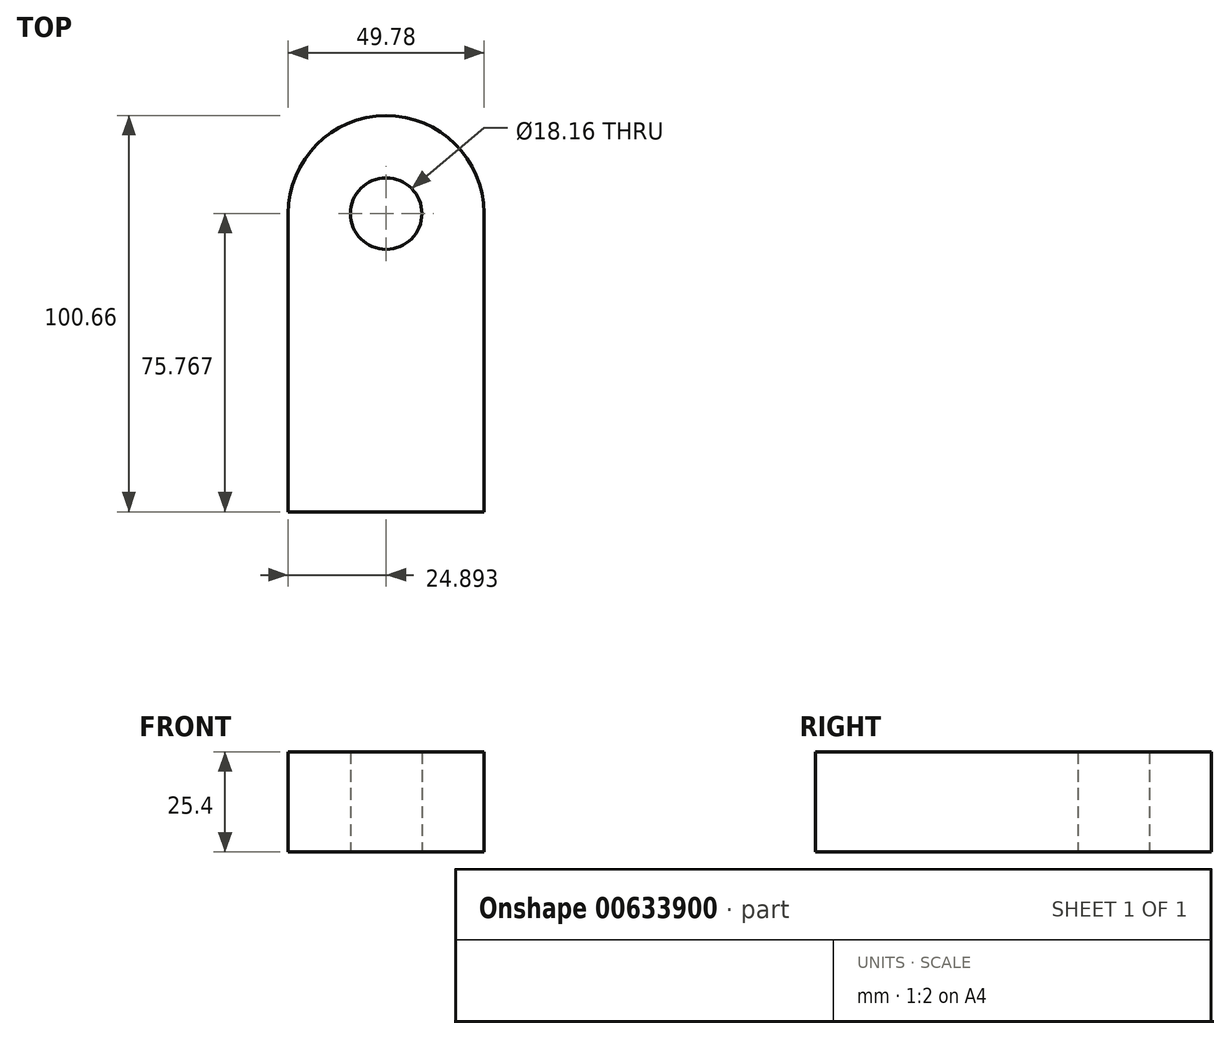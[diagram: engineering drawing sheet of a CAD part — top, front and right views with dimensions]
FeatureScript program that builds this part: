
annotation { "Feature Type Name" : "Feature", "Feature Type Description" : "" }
export const myFeature = defineFeature(function(context is Context, id is Id, definition is map)
    precondition{}
    {
        {
            var Q0;
            Q0=qCreatedBy(makeId("Top.planeOp"),FACE);
            var sketch = newSketch(context, id + "F0", { "sketchPlane" : qUnion([Q0])});
            skLineSegment(sketch, "E0", {"start": v(-27.75, 32.9) * mm, "end": v(-27.75, -42.86) * mm});
            skLineSegment(sketch, "E1", {"start": v(-27.75, -42.86) * mm, "end": v(22.03, -42.86) * mm});
            skLineSegment(sketch, "E2", {"start": v(22.03, -42.86) * mm, "end": v(22.03, 33.1) * mm});
            skLineSegment(sketch, "E3", {"start": v(22.03, 33.1) * mm, "end": v(-27.75, 32.9) * mm});
            skArc(sketch, "E4", {"start": v(22.03, 33.1) * mm, "mid": v(-2.95, 57.8) * mm, "end": v(-27.75, 32.9) * mm});
            skCircle(sketch, "E5", {"center": v(-2.86, 32.9) * mm, "radius": 9.08 * mm});
            skSolve(sketch);
        }
        {
            var Q0;
            {var subQ5=sQuery(id+"F0.wireOp",EDGE,"E0");Q0=makeQuery(id+"F0.imprint","IMPRINT",FACE,{"disambiguationData":[TD([[makeQuery(id+"F0.imprint","IMPRINT",EDGE,{"derivedFrom":subQ5}),1.0]])]});}
            var Q1;
            {var subQ0=sQuery(id+"F0.wireOp",EDGE,"E4");Q1=makeQuery(id+"F0.imprint","IMPRINT",FACE,{"disambiguationData":[TD([[makeQuery(id+"F0.imprint","IMPRINT",EDGE,{"derivedFrom":subQ0}),1.0]])]});}
            extrude(context, id + "F1", {"entities" : qUnion([Q0, Q1]), "depth" : 25.4 * mm, "offsetDistance" : 25.4 * mm});
        }
    });
